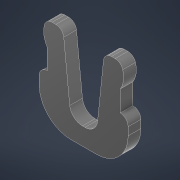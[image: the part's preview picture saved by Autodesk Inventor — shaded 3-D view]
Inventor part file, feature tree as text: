
AUTODESK INVENTOR PART (.ipt)
format: ipt  version: 2021 (Build 250183000, 183)  size: 156,160 bytes
history: native  units: mm
features: other x4, fillet x2, plane x1, extrude x1, reference x1
ambient origin geometry x8: Origin, YZ Plane, XZ Plane, XY Plane, X Axis, Y Axis, Z Axis, Center Point
bodies: Body1 (feature_tree)
feature tree (9):
  other  "clip_sketch"
  plane  "Work Plane1"
  extrude  "clip"  Depth=0.2mm
  fillet  "teeth"  Radius=0.2mm
  fillet  "inside"  Radius=1.0mm
  reference  "Reference3"
  parser-record x1  (decoder bookkeeping rows leaked as tree rows — omitted from the tree; the rows remain in map.json)
  other  "mount_battery.iam"
  other  "mount_battery_fastener:1"
note: 1 file-system path scrubbed to <path> (originals preserved in map.json)
